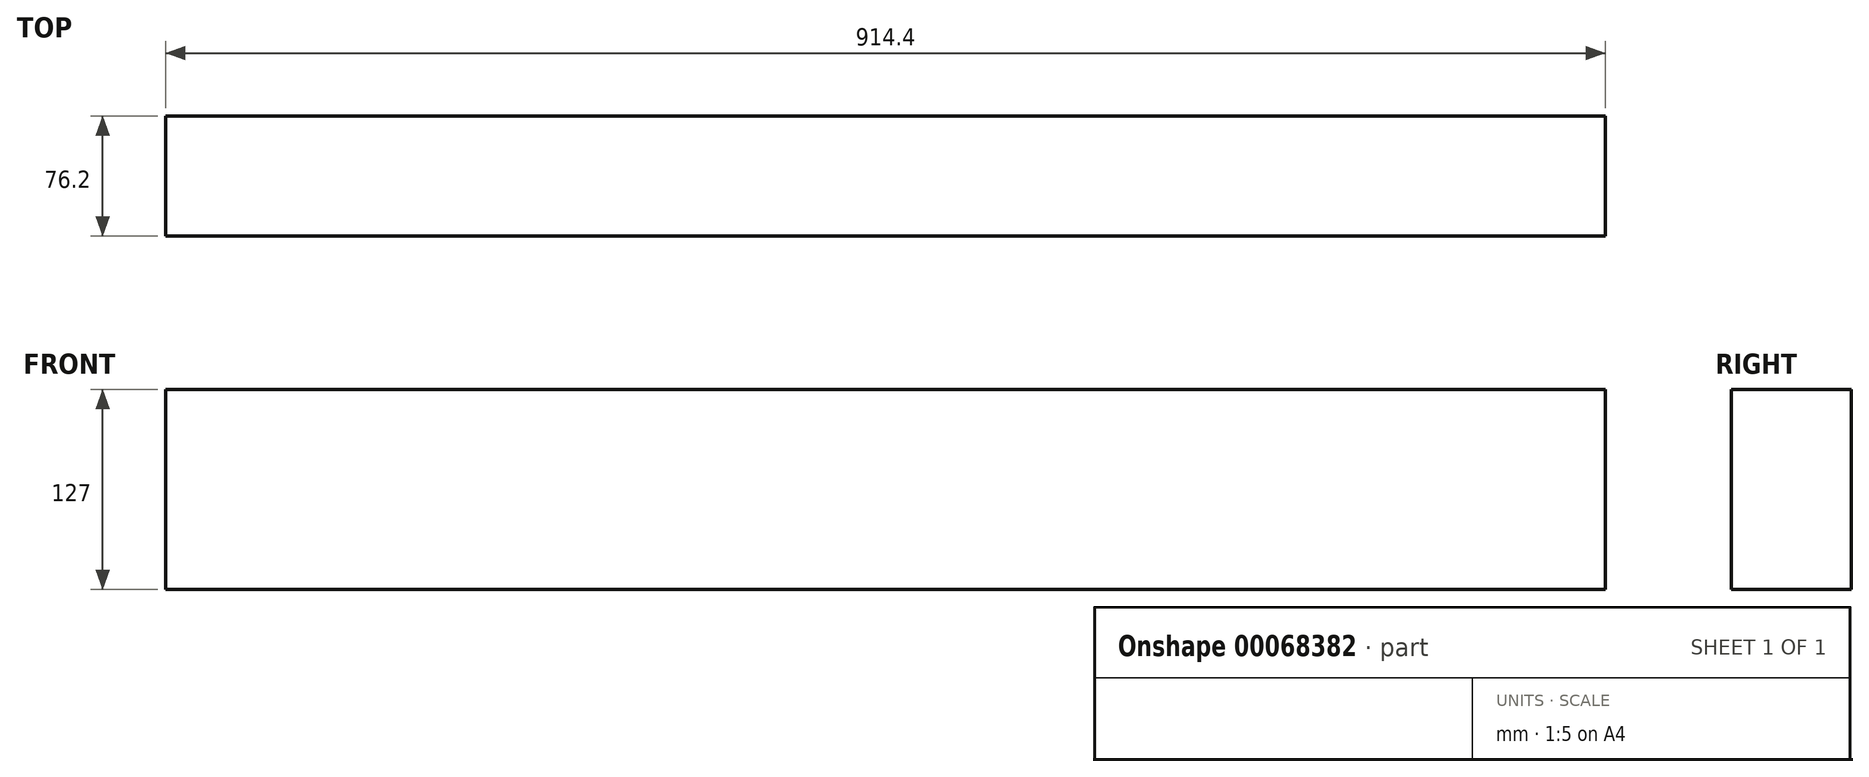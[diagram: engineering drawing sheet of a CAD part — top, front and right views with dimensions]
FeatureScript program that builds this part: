
annotation { "Feature Type Name" : "Feature", "Feature Type Description" : "" }
export const myFeature = defineFeature(function(context is Context, id is Id, definition is map)
    precondition{}
    {
        {
            var Q0;
            Q0=qCreatedBy(makeId("Front.planeOp"),FACE);
            var sketch = newSketch(context, id + "F0", { "sketchPlane" : qUnion([Q0])});
            skLineSegment(sketch, "E0.rect.bottom", {"start": v(457.2, 63.5) * mm, "end": v(-457.2, 63.5) * mm});
            skLineSegment(sketch, "E0.rect.top", {"start": v(457.2, -63.5) * mm, "end": v(-457.2, -63.5) * mm});
            skLineSegment(sketch, "E0.rect.left", {"start": v(457.2, 63.5) * mm, "end": v(457.2, -63.5) * mm});
            skLineSegment(sketch, "E0.rect.right", {"start": v(-457.2, 63.5) * mm, "end": v(-457.2, -63.5) * mm});
            skPoint(sketch, "E0.rect.middle", {"position": v(0, 0) * mm});
            skSolve(sketch);
        }
        {
            var Q0;
            Q0=makeQuery(id+"F0.imprint","IMPRINT",FACE,{"disambiguationData":[TD([[makeQuery(id+"F0.imprint","IMPRINT",EDGE,{"derivedFrom":sQuery(id+"F0.wireOp",EDGE,"E0.rect.bottom")}),1.0]])]});
            extrude(context, id + "F1", {"entities" : qUnion([Q0]), "depth" : 76.2 * mm});
        }
    });
